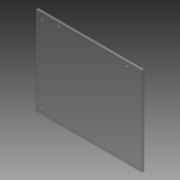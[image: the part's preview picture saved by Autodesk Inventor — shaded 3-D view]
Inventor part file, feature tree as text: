
AUTODESK INVENTOR PART (.ipt)
format: ipt  version: 2014 SP1 (Build 180222100, 222)  size: 83,456 bytes
history: native  units: in
note: dims shown in document units (in); Inventor stores cm internally (conversion verified against a paired STEP export)
features: reference x2, extrude x1, sketch x1
ambient origin geometry x8: Origin, YZ Plane, XZ Plane, XY Plane, X Axis, Y Axis, Z Axis, Center Point
bodies: Solid1 (feature_tree)
feature tree (4):
  extrude  "Extrusion1"  Depth=6.0in
  sketch  "Sketch1"  dims[d0=5.0in d1=6.0in d2=0.125in d3=0.0in d4=0.2in d5=0.15in d6=1.25in d7=0.875in]
  reference  "Reference1"
  reference  "Reference2"
